# Revit family: Haworth_Pebble_Ottoman_AP_PRELIMINARY
name_source: partatom
category: Furniture
revit_build: Autodesk Revit 2018 (Build: 20170223_1515(x64)
units: mm (PartAtom-declared; Revit-internal decimal feet)

## family parameters
Always vertical = Yes
Cut with Voids When Loaded = No
OmniClass Number = 23.40.70.14.64.21
OmniClass Title = Systems Furniture
Room Calculation Point = No
Shared = No
Work Plane-Based = No

## types (4) — shared parameters
Actual Height = 430 mm
Assembly Code = E2020200
Custom Size = No
Custom Width = No
Description = Haworth - Lounge - Pebble - Ottoman
Manufacturer = Haworth
Max. Depth = 1200 mm
Max. Width = 1700 mm  [stored 5.57743 ft]
Min. Depth = 650 mm  [stored 2.13255 ft]
Min. Width = 650 mm  [stored 2.13255 ft]
Model = SEPEXX
Revision Number = 1
Size = Verify Final Dim. w/ Haworth
Trim Finish = Haworth _ Paint _ Plaster
URL = https://www.haworth.com
URL - Product = https://www.haworth.com
Warranty = http://www.haworth.com

## per-type parameters (varying)
| type | Actual Depth | Actual Width | Depth | Large Square | Medium Square | Rectangle | Small Square | Width |
| 850 x 850 | 850 mm | 850 mm | 850 mm | No | Yes | No | No | 850 mm |
| 1200 x 1200 | 1200 mm | 1200 mm | 1200 mm | Yes | No | No | No | 1200 mm |
| 1700 x 850 | 850 mm | 1700 mm  [stored 5.57743 ft] | 850 mm | No | No | Yes | No | 1700 mm  [stored 5.57743 ft] |
| 650 x 650 | 650 mm  [stored 2.13255 ft] | 650 mm  [stored 2.13255 ft] | 650 mm  [stored 2.13255 ft] | No | No | No | Yes | 650 mm  [stored 2.13255 ft] |

note: [stored X ft] marks values corroborated as IEEE doubles in the binary element streams (Revit-internal decimal feet)

## geometry (parser evidence)
native form markers: Sweep x3
no freeform markers — native parametric forms only
